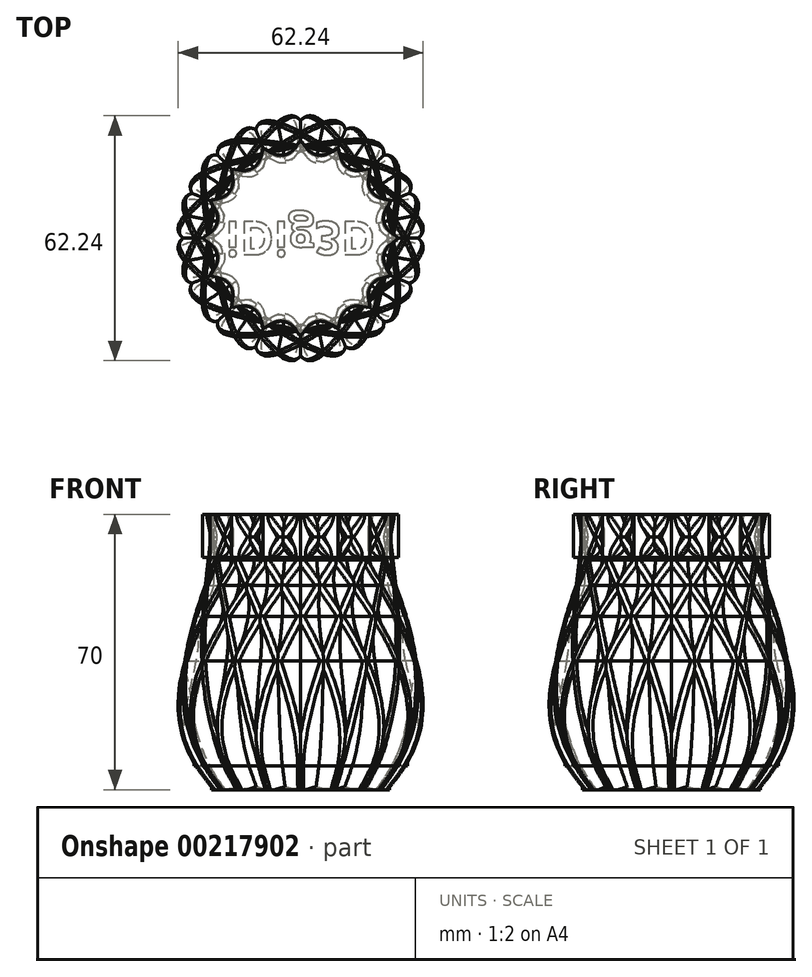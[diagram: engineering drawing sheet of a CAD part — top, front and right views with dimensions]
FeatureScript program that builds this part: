
annotation { "Feature Type Name" : "Feature", "Feature Type Description" : "" }
export const myFeature = defineFeature(function(context is Context, id is Id, definition is map)
    precondition{}
    {
        {
            var Q0;
            Q0=qCreatedBy(makeId("Top.planeOp"),FACE);
            var sketch = newSketch(context, id + "F0", { "sketchPlane" : qUnion([Q0])});
            skLineSegment(sketch, "E0", {"start": v(0, -22.6) * mm, "end": v(3.57, -17.95) * mm});
            skLineSegment(sketch, "E1.MirrorCS", {"start": v(0, -22.6) * mm, "end": v(-3.57, -17.95) * mm});
            skLineSegment(sketch, "E2", {"start": v(-2, -20) * mm, "end": v(2, -20) * mm, "construction": true});
            skPoint(sketch, "E3.orphan", {"position": v(2, -20) * mm});
            skPoint(sketch, "E4.orphan", {"position": v(-2, -20) * mm});
            skLineSegment(sketch, "E5.1.0", {"start": v(8.65, -20.89) * mm, "end": v(3.57, -17.95) * mm});
            skLineSegment(sketch, "E5.1.1", {"start": v(8.65, -20.89) * mm, "end": v(10.17, -15.22) * mm});
            skPoint(sketch, "E5.1.2", {"position": v(5.8, -19.24) * mm});
            skPoint(sketch, "E5.1.3", {"position": v(9.5, -17.71) * mm});
            skLineSegment(sketch, "E5.2.0", {"start": v(15.99, -15.99) * mm, "end": v(10.17, -15.22) * mm});
            skLineSegment(sketch, "E5.2.1", {"start": v(15.99, -15.99) * mm, "end": v(15.22, -10.17) * mm});
            skPoint(sketch, "E5.2.2", {"position": v(12.73, -15.56) * mm});
            skPoint(sketch, "E5.2.3", {"position": v(15.56, -12.73) * mm});
            skLineSegment(sketch, "E5.3.0", {"start": v(20.89, -8.65) * mm, "end": v(15.22, -10.17) * mm});
            skLineSegment(sketch, "E5.3.1", {"start": v(20.89, -8.65) * mm, "end": v(17.95, -3.57) * mm});
            skPoint(sketch, "E5.3.2", {"position": v(17.71, -9.5) * mm});
            skPoint(sketch, "E5.3.3", {"position": v(19.24, -5.8) * mm});
            skLineSegment(sketch, "E5.4.0", {"start": v(22.6, 0) * mm, "end": v(17.95, -3.57) * mm});
            skLineSegment(sketch, "E5.4.1", {"start": v(22.6, 0) * mm, "end": v(17.95, 3.57) * mm});
            skPoint(sketch, "E5.4.2", {"position": v(20, -2) * mm});
            skPoint(sketch, "E5.4.3", {"position": v(20, 2) * mm});
            skLineSegment(sketch, "E5.5.0", {"start": v(20.89, 8.65) * mm, "end": v(17.95, 3.57) * mm});
            skLineSegment(sketch, "E5.5.1", {"start": v(20.89, 8.65) * mm, "end": v(15.22, 10.17) * mm});
            skPoint(sketch, "E5.5.2", {"position": v(19.24, 5.8) * mm});
            skPoint(sketch, "E5.5.3", {"position": v(17.71, 9.5) * mm});
            skLineSegment(sketch, "E5.6.0", {"start": v(15.99, 15.99) * mm, "end": v(15.22, 10.17) * mm});
            skLineSegment(sketch, "E5.6.1", {"start": v(15.99, 15.99) * mm, "end": v(10.17, 15.22) * mm});
            skPoint(sketch, "E5.6.2", {"position": v(15.56, 12.73) * mm});
            skPoint(sketch, "E5.6.3", {"position": v(12.73, 15.56) * mm});
            skLineSegment(sketch, "E5.7.0", {"start": v(8.65, 20.89) * mm, "end": v(10.17, 15.22) * mm});
            skLineSegment(sketch, "E5.7.1", {"start": v(8.65, 20.89) * mm, "end": v(3.57, 17.95) * mm});
            skPoint(sketch, "E5.7.2", {"position": v(9.5, 17.71) * mm});
            skPoint(sketch, "E5.7.3", {"position": v(5.8, 19.24) * mm});
            skLineSegment(sketch, "E5.8.0", {"start": v(0, 22.6) * mm, "end": v(3.57, 17.95) * mm});
            skLineSegment(sketch, "E5.8.1", {"start": v(0, 22.6) * mm, "end": v(-3.57, 17.95) * mm});
            skPoint(sketch, "E5.8.2", {"position": v(2, 20) * mm});
            skPoint(sketch, "E5.8.3", {"position": v(-2, 20) * mm});
            skLineSegment(sketch, "E5.9.0", {"start": v(-8.65, 20.89) * mm, "end": v(-3.57, 17.95) * mm});
            skLineSegment(sketch, "E5.9.1", {"start": v(-8.65, 20.89) * mm, "end": v(-10.17, 15.22) * mm});
            skPoint(sketch, "E5.9.2", {"position": v(-5.8, 19.24) * mm});
            skPoint(sketch, "E5.9.3", {"position": v(-9.5, 17.71) * mm});
            skLineSegment(sketch, "E5.10.0", {"start": v(-15.99, 15.99) * mm, "end": v(-10.17, 15.22) * mm});
            skLineSegment(sketch, "E5.10.1", {"start": v(-15.99, 15.99) * mm, "end": v(-15.22, 10.17) * mm});
            skPoint(sketch, "E5.10.2", {"position": v(-12.73, 15.56) * mm});
            skPoint(sketch, "E5.10.3", {"position": v(-15.56, 12.73) * mm});
            skLineSegment(sketch, "E5.11.0", {"start": v(-20.89, 8.65) * mm, "end": v(-15.22, 10.17) * mm});
            skLineSegment(sketch, "E5.11.1", {"start": v(-20.89, 8.65) * mm, "end": v(-17.95, 3.57) * mm});
            skPoint(sketch, "E5.11.2", {"position": v(-17.71, 9.5) * mm});
            skPoint(sketch, "E5.11.3", {"position": v(-19.24, 5.8) * mm});
            skLineSegment(sketch, "E5.12.0", {"start": v(-22.6, 0) * mm, "end": v(-17.95, 3.57) * mm});
            skLineSegment(sketch, "E5.12.1", {"start": v(-22.6, 0) * mm, "end": v(-17.95, -3.57) * mm});
            skPoint(sketch, "E5.12.2", {"position": v(-20, 2) * mm});
            skPoint(sketch, "E5.12.3", {"position": v(-20, -2) * mm});
            skLineSegment(sketch, "E5.13.0", {"start": v(-20.89, -8.65) * mm, "end": v(-17.95, -3.57) * mm});
            skLineSegment(sketch, "E5.13.1", {"start": v(-20.89, -8.65) * mm, "end": v(-15.22, -10.17) * mm});
            skPoint(sketch, "E5.13.2", {"position": v(-19.24, -5.8) * mm});
            skPoint(sketch, "E5.13.3", {"position": v(-17.71, -9.5) * mm});
            skLineSegment(sketch, "E5.14.0", {"start": v(-15.99, -15.99) * mm, "end": v(-15.22, -10.17) * mm});
            skLineSegment(sketch, "E5.14.1", {"start": v(-15.99, -15.99) * mm, "end": v(-10.17, -15.22) * mm});
            skPoint(sketch, "E5.14.2", {"position": v(-15.56, -12.73) * mm});
            skPoint(sketch, "E5.14.3", {"position": v(-12.73, -15.56) * mm});
            skLineSegment(sketch, "E5.15.0", {"start": v(-8.65, -20.89) * mm, "end": v(-10.17, -15.22) * mm});
            skLineSegment(sketch, "E5.15.1", {"start": v(-8.65, -20.89) * mm, "end": v(-3.57, -17.95) * mm});
            skPoint(sketch, "E5.15.2", {"position": v(-9.5, -17.71) * mm});
            skPoint(sketch, "E5.15.3", {"position": v(-5.8, -19.24) * mm});
            skPoint(sketch, "E5.center", {"position": v(0, 0) * mm});
            skSolve(sketch);
        }
        {
            var Q0;
            Q0=qSketchRegion(id+"F0",true);
            var Q1;
            Q1=sQuery(id+"F0.wireOp",EDGE,"1b0f9fb0-313e-4c25-a7f3-239414019b98.12.0");
            var Q2;
            Q2=sQuery(id+"F0.wireOp",EDGE,"1b0f9fb0-313e-4c25-a7f3-239414019b98.13.0");
            var Q3;
            Q3=sQuery(id+"F0.wireOp",EDGE,"1b0f9fb0-313e-4c25-a7f3-239414019b98.14.0");
            var Q4;
            Q4=sQuery(id+"F0.wireOp",EDGE,"cSzGq71W-xBtn-32TR-Fl9i-aVuZMrbFhdef");
            var Q5;
            Q5=sQuery(id+"F0.wireOp",EDGE,"1b0f9fb0-313e-4c25-a7f3-239414019b98.1.0");
            var Q6;
            Q6=sQuery(id+"F0.wireOp",EDGE,"1b0f9fb0-313e-4c25-a7f3-239414019b98.2.0");
            var Q7;
            Q7=sQuery(id+"F0.wireOp",EDGE,"1b0f9fb0-313e-4c25-a7f3-239414019b98.3.0");
            var Q8;
            Q8=sQuery(id+"F0.wireOp",EDGE,"1b0f9fb0-313e-4c25-a7f3-239414019b98.4.0");
            var Q9;
            Q9=sQuery(id+"F0.wireOp",EDGE,"1b0f9fb0-313e-4c25-a7f3-239414019b98.5.0");
            var Q10;
            Q10=sQuery(id+"F0.wireOp",EDGE,"1b0f9fb0-313e-4c25-a7f3-239414019b98.6.0");
            var Q11;
            Q11=sQuery(id+"F0.wireOp",EDGE,"1b0f9fb0-313e-4c25-a7f3-239414019b98.7.0");
            var Q12;
            Q12=sQuery(id+"F0.wireOp",EDGE,"1b0f9fb0-313e-4c25-a7f3-239414019b98.8.0");
            var Q13;
            Q13=sQuery(id+"F0.wireOp",EDGE,"1b0f9fb0-313e-4c25-a7f3-239414019b98.9.0");
            var Q14;
            Q14=sQuery(id+"F0.wireOp",EDGE,"1b0f9fb0-313e-4c25-a7f3-239414019b98.10.0");
            var Q15;
            Q15=sQuery(id+"F0.wireOp",EDGE,"1b0f9fb0-313e-4c25-a7f3-239414019b98.11.0");
            var Q16;
            Q16=sQuery(id+"F0.wireOp",EDGE,"1b0f9fb0-313e-4c25-a7f3-239414019b98.15.0");
            var Q17;
            Q17=sQuery(id+"F0.wireOp",EDGE,"jFGbZxWp-MTVa-Zhwl-fwm2-ItDZcObQq6kR");
            extrude(context, id + "F1", {"entities" : qUnion([Q0]), "surfaceEntities" : qUnion([Q1, Q2, Q3, Q4, Q5, Q6, Q7, Q8, Q9, Q10, Q11, Q12, Q13, Q14, Q15, Q16, Q17]), "depth" : 10 * mm});
        }
        {
            var Q0;
            Q0=makeQuery(id+"F1.opExtrude","SWEPT_EDGE",EDGE,{"disambiguationData":[OSD([sQuery(id+"F0.wireOp",EDGE,"E5.9.1"),sQuery(id+"F0.wireOp",EDGE,"E5.10.0")])]});
            var Q1;
            Q1=makeQuery(id+"F1.opExtrude","SWEPT_EDGE",EDGE,{"disambiguationData":[OSD([sQuery(id+"F0.wireOp",EDGE,"E5.10.1"),sQuery(id+"F0.wireOp",EDGE,"E5.11.0")])]});
            var Q2;
            Q2=makeQuery(id+"F1.opExtrude","SWEPT_EDGE",EDGE,{"disambiguationData":[OSD([sQuery(id+"F0.wireOp",EDGE,"E5.8.1"),sQuery(id+"F0.wireOp",EDGE,"E5.9.0")])]});
            var Q3;
            Q3=makeQuery(id+"F1.opExtrude","SWEPT_EDGE",EDGE,{"disambiguationData":[OSD([sQuery(id+"F0.wireOp",EDGE,"E5.7.1"),sQuery(id+"F0.wireOp",EDGE,"E5.8.0")])]});
            var Q4;
            Q4=makeQuery(id+"F1.opExtrude","SWEPT_EDGE",EDGE,{"disambiguationData":[OSD([sQuery(id+"F0.wireOp",EDGE,"E5.6.1"),sQuery(id+"F0.wireOp",EDGE,"E5.7.0")])]});
            var Q5;
            Q5=makeQuery(id+"F1.opExtrude","SWEPT_EDGE",EDGE,{"disambiguationData":[OSD([sQuery(id+"F0.wireOp",EDGE,"E5.5.1"),sQuery(id+"F0.wireOp",EDGE,"E5.6.0")])]});
            var Q6;
            Q6=makeQuery(id+"F1.opExtrude","SWEPT_EDGE",EDGE,{"disambiguationData":[OSD([sQuery(id+"F0.wireOp",EDGE,"E5.4.1"),sQuery(id+"F0.wireOp",EDGE,"E5.5.0")])]});
            var Q7;
            Q7=makeQuery(id+"F1.opExtrude","SWEPT_EDGE",EDGE,{"disambiguationData":[OSD([sQuery(id+"F0.wireOp",EDGE,"E5.3.1"),sQuery(id+"F0.wireOp",EDGE,"E5.4.0")])]});
            var Q8;
            Q8=makeQuery(id+"F1.opExtrude","SWEPT_EDGE",EDGE,{"disambiguationData":[OSD([sQuery(id+"F0.wireOp",EDGE,"E5.2.1"),sQuery(id+"F0.wireOp",EDGE,"E5.3.0")])]});
            var Q9;
            Q9=makeQuery(id+"F1.opExtrude","SWEPT_EDGE",EDGE,{"disambiguationData":[OSD([sQuery(id+"F0.wireOp",EDGE,"E0"),sQuery(id+"F0.wireOp",EDGE,"E5.1.0")])]});
            var Q10;
            Q10=makeQuery(id+"F1.opExtrude","SWEPT_EDGE",EDGE,{"disambiguationData":[OSD([sQuery(id+"F0.wireOp",EDGE,"E1.MirrorCS"),sQuery(id+"F0.wireOp",EDGE,"E5.15.1")])]});
            var Q11;
            Q11=makeQuery(id+"F1.opExtrude","SWEPT_EDGE",EDGE,{"disambiguationData":[OSD([sQuery(id+"F0.wireOp",EDGE,"E5.14.1"),sQuery(id+"F0.wireOp",EDGE,"E5.15.0")])]});
            var Q12;
            Q12=makeQuery(id+"F1.opExtrude","SWEPT_EDGE",EDGE,{"disambiguationData":[OSD([sQuery(id+"F0.wireOp",EDGE,"E5.13.1"),sQuery(id+"F0.wireOp",EDGE,"E5.14.0")])]});
            var Q13;
            Q13=makeQuery(id+"F1.opExtrude","SWEPT_EDGE",EDGE,{"disambiguationData":[OSD([sQuery(id+"F0.wireOp",EDGE,"E5.12.1"),sQuery(id+"F0.wireOp",EDGE,"E5.13.0")])]});
            var Q14;
            Q14=makeQuery(id+"F1.opExtrude","SWEPT_EDGE",EDGE,{"disambiguationData":[OSD([sQuery(id+"F0.wireOp",EDGE,"E5.11.1"),sQuery(id+"F0.wireOp",EDGE,"E5.12.0")])]});
            var Q15;
            Q15=makeQuery(id+"F1.opExtrude","SWEPT_EDGE",EDGE,{"disambiguationData":[OSD([sQuery(id+"F0.wireOp",EDGE,"E5.1.1"),sQuery(id+"F0.wireOp",EDGE,"E5.2.0")])]});
            fillet(context, id + "F2", {"entities" : qUnion([Q0, Q1, Q2, Q3, Q4, Q5, Q6, Q7, Q8, Q9, Q10, Q11, Q12, Q13, Q14, Q15]), "radius" : 4 * mm, "tangentPropagation" : true, "allowEdgeOverflow" : false});
        }
        {
            var Q0;
            Q0=makeQuery(id+"F1.opExtrude","SWEPT_BODY",BODY,{"disambiguationData":[OSD([sQuery(id+"F0.wireOp",EDGE,"E0"),sQuery(id+"F0.wireOp",EDGE,"E1.MirrorCS"),sQuery(id+"F0.wireOp",EDGE,"E5.1.0"),sQuery(id+"F0.wireOp",EDGE,"E5.1.1"),sQuery(id+"F0.wireOp",EDGE,"E5.2.0"),sQuery(id+"F0.wireOp",EDGE,"E5.2.1"),sQuery(id+"F0.wireOp",EDGE,"E5.3.0"),sQuery(id+"F0.wireOp",EDGE,"E5.3.1"),sQuery(id+"F0.wireOp",EDGE,"E5.4.0"),sQuery(id+"F0.wireOp",EDGE,"E5.4.1"),sQuery(id+"F0.wireOp",EDGE,"E5.5.0"),sQuery(id+"F0.wireOp",EDGE,"E5.5.1"),sQuery(id+"F0.wireOp",EDGE,"E5.6.0"),sQuery(id+"F0.wireOp",EDGE,"E5.6.1"),sQuery(id+"F0.wireOp",EDGE,"E5.7.0"),sQuery(id+"F0.wireOp",EDGE,"E5.7.1"),sQuery(id+"F0.wireOp",EDGE,"E5.8.0"),sQuery(id+"F0.wireOp",EDGE,"E5.8.1"),sQuery(id+"F0.wireOp",EDGE,"E5.9.0"),sQuery(id+"F0.wireOp",EDGE,"E5.9.1"),sQuery(id+"F0.wireOp",EDGE,"E5.10.0"),sQuery(id+"F0.wireOp",EDGE,"E5.10.1"),sQuery(id+"F0.wireOp",EDGE,"E5.11.0"),sQuery(id+"F0.wireOp",EDGE,"E5.11.1"),sQuery(id+"F0.wireOp",EDGE,"E5.12.0"),sQuery(id+"F0.wireOp",EDGE,"E5.12.1"),sQuery(id+"F0.wireOp",EDGE,"E5.13.0"),sQuery(id+"F0.wireOp",EDGE,"E5.13.1"),sQuery(id+"F0.wireOp",EDGE,"E5.14.0"),sQuery(id+"F0.wireOp",EDGE,"E5.14.1"),sQuery(id+"F0.wireOp",EDGE,"E5.15.0"),sQuery(id+"F0.wireOp",EDGE,"E5.15.1")])]});
            transform(context, id + "F3", {"entities" : qUnion([Q0]), "transformType" : TransformType.TRANSLATION_3D, "dx" : 0 * mm, "dy" : 0 * mm, "dz" : 5 * mm, "makeCopy" : true});
        }
        {
            var Q0;
            Q0=makeQuery(id+"F3.opPattern","COPY",BODY,{"derivedFrom":makeQuery(id+"F1.opExtrude","SWEPT_BODY",BODY,{"disambiguationData":[OSD([sQuery(id+"F0.wireOp",EDGE,"E0"),sQuery(id+"F0.wireOp",EDGE,"E1.MirrorCS"),sQuery(id+"F0.wireOp",EDGE,"E5.1.0"),sQuery(id+"F0.wireOp",EDGE,"E5.1.1"),sQuery(id+"F0.wireOp",EDGE,"E5.2.0"),sQuery(id+"F0.wireOp",EDGE,"E5.2.1"),sQuery(id+"F0.wireOp",EDGE,"E5.3.0"),sQuery(id+"F0.wireOp",EDGE,"E5.3.1"),sQuery(id+"F0.wireOp",EDGE,"E5.4.0"),sQuery(id+"F0.wireOp",EDGE,"E5.4.1"),sQuery(id+"F0.wireOp",EDGE,"E5.5.0"),sQuery(id+"F0.wireOp",EDGE,"E5.5.1"),sQuery(id+"F0.wireOp",EDGE,"E5.6.0"),sQuery(id+"F0.wireOp",EDGE,"E5.6.1"),sQuery(id+"F0.wireOp",EDGE,"E5.7.0"),sQuery(id+"F0.wireOp",EDGE,"E5.7.1"),sQuery(id+"F0.wireOp",EDGE,"E5.8.0"),sQuery(id+"F0.wireOp",EDGE,"E5.8.1"),sQuery(id+"F0.wireOp",EDGE,"E5.9.0"),sQuery(id+"F0.wireOp",EDGE,"E5.9.1"),sQuery(id+"F0.wireOp",EDGE,"E5.10.0"),sQuery(id+"F0.wireOp",EDGE,"E5.10.1"),sQuery(id+"F0.wireOp",EDGE,"E5.11.0"),sQuery(id+"F0.wireOp",EDGE,"E5.11.1"),sQuery(id+"F0.wireOp",EDGE,"E5.12.0"),sQuery(id+"F0.wireOp",EDGE,"E5.12.1"),sQuery(id+"F0.wireOp",EDGE,"E5.13.0"),sQuery(id+"F0.wireOp",EDGE,"E5.13.1"),sQuery(id+"F0.wireOp",EDGE,"E5.14.0"),sQuery(id+"F0.wireOp",EDGE,"E5.14.1"),sQuery(id+"F0.wireOp",EDGE,"E5.15.0"),sQuery(id+"F0.wireOp",EDGE,"E5.15.1")])]}),"instanceName":"1"});
            var Q1;
            Q1=qCreatedBy(makeId("Origin.pointOp"),VERTEX);
            transform(context, id + "F4", {"entities" : qUnion([Q0]), "transformType" : TransformType.SCALE_UNIFORMLY, "scale" : 1.2, "scalePoint" : qUnion([Q1]), "makeCopy" : false});
        }
        {
            var Q0;
            Q0=makeQuery(id+"F1.opExtrude","SWEPT_BODY",BODY,{"disambiguationData":[OSD([sQuery(id+"F0.wireOp",EDGE,"E0"),sQuery(id+"F0.wireOp",EDGE,"E1.MirrorCS"),sQuery(id+"F0.wireOp",EDGE,"E5.1.0"),sQuery(id+"F0.wireOp",EDGE,"E5.1.1"),sQuery(id+"F0.wireOp",EDGE,"E5.2.0"),sQuery(id+"F0.wireOp",EDGE,"E5.2.1"),sQuery(id+"F0.wireOp",EDGE,"E5.3.0"),sQuery(id+"F0.wireOp",EDGE,"E5.3.1"),sQuery(id+"F0.wireOp",EDGE,"E5.4.0"),sQuery(id+"F0.wireOp",EDGE,"E5.4.1"),sQuery(id+"F0.wireOp",EDGE,"E5.5.0"),sQuery(id+"F0.wireOp",EDGE,"E5.5.1"),sQuery(id+"F0.wireOp",EDGE,"E5.6.0"),sQuery(id+"F0.wireOp",EDGE,"E5.6.1"),sQuery(id+"F0.wireOp",EDGE,"E5.7.0"),sQuery(id+"F0.wireOp",EDGE,"E5.7.1"),sQuery(id+"F0.wireOp",EDGE,"E5.8.0"),sQuery(id+"F0.wireOp",EDGE,"E5.8.1"),sQuery(id+"F0.wireOp",EDGE,"E5.9.0"),sQuery(id+"F0.wireOp",EDGE,"E5.9.1"),sQuery(id+"F0.wireOp",EDGE,"E5.10.0"),sQuery(id+"F0.wireOp",EDGE,"E5.10.1"),sQuery(id+"F0.wireOp",EDGE,"E5.11.0"),sQuery(id+"F0.wireOp",EDGE,"E5.11.1"),sQuery(id+"F0.wireOp",EDGE,"E5.12.0"),sQuery(id+"F0.wireOp",EDGE,"E5.12.1"),sQuery(id+"F0.wireOp",EDGE,"E5.13.0"),sQuery(id+"F0.wireOp",EDGE,"E5.13.1"),sQuery(id+"F0.wireOp",EDGE,"E5.14.0"),sQuery(id+"F0.wireOp",EDGE,"E5.14.1"),sQuery(id+"F0.wireOp",EDGE,"E5.15.0"),sQuery(id+"F0.wireOp",EDGE,"E5.15.1")])]});
            transform(context, id + "F5", {"entities" : qUnion([Q0]), "transformType" : TransformType.TRANSLATION_3D, "dx" : 0 * mm, "dy" : 0 * mm, "dz" : 60 * mm, "makeCopy" : true});
        }
        {
            var Q0;
            Q0=makeQuery(id+"F5.opPattern","COPY",FACE,{"derivedFrom":makeQuery(id+"F1.opExtrude","CAP_FACE",FACE,{"disambiguationData":[OSD([sQuery(id+"F0.wireOp",EDGE,"E0"),sQuery(id+"F0.wireOp",EDGE,"E1.MirrorCS"),sQuery(id+"F0.wireOp",EDGE,"E5.1.0"),sQuery(id+"F0.wireOp",EDGE,"E5.1.1"),sQuery(id+"F0.wireOp",EDGE,"E5.2.0"),sQuery(id+"F0.wireOp",EDGE,"E5.2.1"),sQuery(id+"F0.wireOp",EDGE,"E5.3.0"),sQuery(id+"F0.wireOp",EDGE,"E5.3.1"),sQuery(id+"F0.wireOp",EDGE,"E5.4.0"),sQuery(id+"F0.wireOp",EDGE,"E5.4.1"),sQuery(id+"F0.wireOp",EDGE,"E5.5.0"),sQuery(id+"F0.wireOp",EDGE,"E5.5.1"),sQuery(id+"F0.wireOp",EDGE,"E5.6.0"),sQuery(id+"F0.wireOp",EDGE,"E5.6.1"),sQuery(id+"F0.wireOp",EDGE,"E5.7.0"),sQuery(id+"F0.wireOp",EDGE,"E5.7.1"),sQuery(id+"F0.wireOp",EDGE,"E5.8.0"),sQuery(id+"F0.wireOp",EDGE,"E5.8.1"),sQuery(id+"F0.wireOp",EDGE,"E5.9.0"),sQuery(id+"F0.wireOp",EDGE,"E5.9.1"),sQuery(id+"F0.wireOp",EDGE,"E5.10.0"),sQuery(id+"F0.wireOp",EDGE,"E5.10.1"),sQuery(id+"F0.wireOp",EDGE,"E5.11.0"),sQuery(id+"F0.wireOp",EDGE,"E5.11.1"),sQuery(id+"F0.wireOp",EDGE,"E5.12.0"),sQuery(id+"F0.wireOp",EDGE,"E5.12.1"),sQuery(id+"F0.wireOp",EDGE,"E5.13.0"),sQuery(id+"F0.wireOp",EDGE,"E5.13.1"),sQuery(id+"F0.wireOp",EDGE,"E5.14.0"),sQuery(id+"F0.wireOp",EDGE,"E5.14.1"),sQuery(id+"F0.wireOp",EDGE,"E5.15.0"),sQuery(id+"F0.wireOp",EDGE,"E5.15.1")])],"isStart":false}),"instanceName":"1"});
            var sketch = newSketch(context, id + "F6", { "sketchPlane" : qUnion([Q0])});
            skPoint(sketch, "E6.0", {"position": v(0, 0) * mm});
            skSolve(sketch);
        }
        {
            var Q0;
            Q0=makeQuery(id+"F5.opPattern","COPY",BODY,{"derivedFrom":makeQuery(id+"F1.opExtrude","SWEPT_BODY",BODY,{"disambiguationData":[OSD([sQuery(id+"F0.wireOp",EDGE,"E0"),sQuery(id+"F0.wireOp",EDGE,"E1.MirrorCS"),sQuery(id+"F0.wireOp",EDGE,"E5.1.0"),sQuery(id+"F0.wireOp",EDGE,"E5.1.1"),sQuery(id+"F0.wireOp",EDGE,"E5.2.0"),sQuery(id+"F0.wireOp",EDGE,"E5.2.1"),sQuery(id+"F0.wireOp",EDGE,"E5.3.0"),sQuery(id+"F0.wireOp",EDGE,"E5.3.1"),sQuery(id+"F0.wireOp",EDGE,"E5.4.0"),sQuery(id+"F0.wireOp",EDGE,"E5.4.1"),sQuery(id+"F0.wireOp",EDGE,"E5.5.0"),sQuery(id+"F0.wireOp",EDGE,"E5.5.1"),sQuery(id+"F0.wireOp",EDGE,"E5.6.0"),sQuery(id+"F0.wireOp",EDGE,"E5.6.1"),sQuery(id+"F0.wireOp",EDGE,"E5.7.0"),sQuery(id+"F0.wireOp",EDGE,"E5.7.1"),sQuery(id+"F0.wireOp",EDGE,"E5.8.0"),sQuery(id+"F0.wireOp",EDGE,"E5.8.1"),sQuery(id+"F0.wireOp",EDGE,"E5.9.0"),sQuery(id+"F0.wireOp",EDGE,"E5.9.1"),sQuery(id+"F0.wireOp",EDGE,"E5.10.0"),sQuery(id+"F0.wireOp",EDGE,"E5.10.1"),sQuery(id+"F0.wireOp",EDGE,"E5.11.0"),sQuery(id+"F0.wireOp",EDGE,"E5.11.1"),sQuery(id+"F0.wireOp",EDGE,"E5.12.0"),sQuery(id+"F0.wireOp",EDGE,"E5.12.1"),sQuery(id+"F0.wireOp",EDGE,"E5.13.0"),sQuery(id+"F0.wireOp",EDGE,"E5.13.1"),sQuery(id+"F0.wireOp",EDGE,"E5.14.0"),sQuery(id+"F0.wireOp",EDGE,"E5.14.1"),sQuery(id+"F0.wireOp",EDGE,"E5.15.0"),sQuery(id+"F0.wireOp",EDGE,"E5.15.1")])]}),"instanceName":"1"});
            var Q1;
            Q1=sQuery(id+"F6.wireOp",VERTEX,"E6.0");
            transform(context, id + "F7", {"entities" : qUnion([Q0]), "transformType" : TransformType.SCALE_UNIFORMLY, "scale" : 1.1, "scalePoint" : qUnion([Q1]), "makeCopy" : false});
        }
        {
            var Q0;
            Q0=makeQuery(id+"F1.opExtrude","CAP_FACE",FACE,{"disambiguationData":[OSD([sQuery(id+"F0.wireOp",EDGE,"E0"),sQuery(id+"F0.wireOp",EDGE,"E1.MirrorCS"),sQuery(id+"F0.wireOp",EDGE,"E5.1.0"),sQuery(id+"F0.wireOp",EDGE,"E5.1.1"),sQuery(id+"F0.wireOp",EDGE,"E5.2.0"),sQuery(id+"F0.wireOp",EDGE,"E5.2.1"),sQuery(id+"F0.wireOp",EDGE,"E5.3.0"),sQuery(id+"F0.wireOp",EDGE,"E5.3.1"),sQuery(id+"F0.wireOp",EDGE,"E5.4.0"),sQuery(id+"F0.wireOp",EDGE,"E5.4.1"),sQuery(id+"F0.wireOp",EDGE,"E5.5.0"),sQuery(id+"F0.wireOp",EDGE,"E5.5.1"),sQuery(id+"F0.wireOp",EDGE,"E5.6.0"),sQuery(id+"F0.wireOp",EDGE,"E5.6.1"),sQuery(id+"F0.wireOp",EDGE,"E5.7.0"),sQuery(id+"F0.wireOp",EDGE,"E5.7.1"),sQuery(id+"F0.wireOp",EDGE,"E5.8.0"),sQuery(id+"F0.wireOp",EDGE,"E5.8.1"),sQuery(id+"F0.wireOp",EDGE,"E5.9.0"),sQuery(id+"F0.wireOp",EDGE,"E5.9.1"),sQuery(id+"F0.wireOp",EDGE,"E5.10.0"),sQuery(id+"F0.wireOp",EDGE,"E5.10.1"),sQuery(id+"F0.wireOp",EDGE,"E5.11.0"),sQuery(id+"F0.wireOp",EDGE,"E5.11.1"),sQuery(id+"F0.wireOp",EDGE,"E5.12.0"),sQuery(id+"F0.wireOp",EDGE,"E5.12.1"),sQuery(id+"F0.wireOp",EDGE,"E5.13.0"),sQuery(id+"F0.wireOp",EDGE,"E5.13.1"),sQuery(id+"F0.wireOp",EDGE,"E5.14.0"),sQuery(id+"F0.wireOp",EDGE,"E5.14.1"),sQuery(id+"F0.wireOp",EDGE,"E5.15.0"),sQuery(id+"F0.wireOp",EDGE,"E5.15.1")])],"isStart":true});
            var Q1;
            Q1=makeQuery(id+"F3.opPattern","COPY",FACE,{"derivedFrom":makeQuery(id+"F1.opExtrude","CAP_FACE",FACE,{"disambiguationData":[OSD([sQuery(id+"F0.wireOp",EDGE,"E0"),sQuery(id+"F0.wireOp",EDGE,"E1.MirrorCS"),sQuery(id+"F0.wireOp",EDGE,"E5.1.0"),sQuery(id+"F0.wireOp",EDGE,"E5.1.1"),sQuery(id+"F0.wireOp",EDGE,"E5.2.0"),sQuery(id+"F0.wireOp",EDGE,"E5.2.1"),sQuery(id+"F0.wireOp",EDGE,"E5.3.0"),sQuery(id+"F0.wireOp",EDGE,"E5.3.1"),sQuery(id+"F0.wireOp",EDGE,"E5.4.0"),sQuery(id+"F0.wireOp",EDGE,"E5.4.1"),sQuery(id+"F0.wireOp",EDGE,"E5.5.0"),sQuery(id+"F0.wireOp",EDGE,"E5.5.1"),sQuery(id+"F0.wireOp",EDGE,"E5.6.0"),sQuery(id+"F0.wireOp",EDGE,"E5.6.1"),sQuery(id+"F0.wireOp",EDGE,"E5.7.0"),sQuery(id+"F0.wireOp",EDGE,"E5.7.1"),sQuery(id+"F0.wireOp",EDGE,"E5.8.0"),sQuery(id+"F0.wireOp",EDGE,"E5.8.1"),sQuery(id+"F0.wireOp",EDGE,"E5.9.0"),sQuery(id+"F0.wireOp",EDGE,"E5.9.1"),sQuery(id+"F0.wireOp",EDGE,"E5.10.0"),sQuery(id+"F0.wireOp",EDGE,"E5.10.1"),sQuery(id+"F0.wireOp",EDGE,"E5.11.0"),sQuery(id+"F0.wireOp",EDGE,"E5.11.1"),sQuery(id+"F0.wireOp",EDGE,"E5.12.0"),sQuery(id+"F0.wireOp",EDGE,"E5.12.1"),sQuery(id+"F0.wireOp",EDGE,"E5.13.0"),sQuery(id+"F0.wireOp",EDGE,"E5.13.1"),sQuery(id+"F0.wireOp",EDGE,"E5.14.0"),sQuery(id+"F0.wireOp",EDGE,"E5.14.1"),sQuery(id+"F0.wireOp",EDGE,"E5.15.0"),sQuery(id+"F0.wireOp",EDGE,"E5.15.1")])],"isStart":true}),"instanceName":"1"});
            var Q2;
            Q2=makeQuery(id+"F5.opPattern","COPY",FACE,{"derivedFrom":makeQuery(id+"F1.opExtrude","CAP_FACE",FACE,{"disambiguationData":[OSD([sQuery(id+"F0.wireOp",EDGE,"E0"),sQuery(id+"F0.wireOp",EDGE,"E1.MirrorCS"),sQuery(id+"F0.wireOp",EDGE,"E5.1.0"),sQuery(id+"F0.wireOp",EDGE,"E5.1.1"),sQuery(id+"F0.wireOp",EDGE,"E5.2.0"),sQuery(id+"F0.wireOp",EDGE,"E5.2.1"),sQuery(id+"F0.wireOp",EDGE,"E5.3.0"),sQuery(id+"F0.wireOp",EDGE,"E5.3.1"),sQuery(id+"F0.wireOp",EDGE,"E5.4.0"),sQuery(id+"F0.wireOp",EDGE,"E5.4.1"),sQuery(id+"F0.wireOp",EDGE,"E5.5.0"),sQuery(id+"F0.wireOp",EDGE,"E5.5.1"),sQuery(id+"F0.wireOp",EDGE,"E5.6.0"),sQuery(id+"F0.wireOp",EDGE,"E5.6.1"),sQuery(id+"F0.wireOp",EDGE,"E5.7.0"),sQuery(id+"F0.wireOp",EDGE,"E5.7.1"),sQuery(id+"F0.wireOp",EDGE,"E5.8.0"),sQuery(id+"F0.wireOp",EDGE,"E5.8.1"),sQuery(id+"F0.wireOp",EDGE,"E5.9.0"),sQuery(id+"F0.wireOp",EDGE,"E5.9.1"),sQuery(id+"F0.wireOp",EDGE,"E5.10.0"),sQuery(id+"F0.wireOp",EDGE,"E5.10.1"),sQuery(id+"F0.wireOp",EDGE,"E5.11.0"),sQuery(id+"F0.wireOp",EDGE,"E5.11.1"),sQuery(id+"F0.wireOp",EDGE,"E5.12.0"),sQuery(id+"F0.wireOp",EDGE,"E5.12.1"),sQuery(id+"F0.wireOp",EDGE,"E5.13.0"),sQuery(id+"F0.wireOp",EDGE,"E5.13.1"),sQuery(id+"F0.wireOp",EDGE,"E5.14.0"),sQuery(id+"F0.wireOp",EDGE,"E5.14.1"),sQuery(id+"F0.wireOp",EDGE,"E5.15.0"),sQuery(id+"F0.wireOp",EDGE,"E5.15.1")])],"isStart":false}),"instanceName":"1"});
            var Q3;
            Q3=sQuery(id+"F0.wireOp",VERTEX,"E5.2.1.start");
            var Q4;
            Q4=makeQuery(id+"F3.opPattern","COPY",VERTEX,{"derivedFrom":makeQuery(id+"F1.opExtrude","CAP_VERTEX",VERTEX,{"disambiguationData":[OSD([sQuery(id+"F0.wireOp",EDGE,"E5.2.0"),sQuery(id+"F0.wireOp",EDGE,"E5.2.1")])],"isStart":true}),"instanceName":"1"});
            var Q5;
            Q5=makeQuery(id+"F5.opPattern","COPY",VERTEX,{"derivedFrom":makeQuery(id+"F1.opExtrude","CAP_VERTEX",VERTEX,{"disambiguationData":[OSD([sQuery(id+"F0.wireOp",EDGE,"E5.15.0"),sQuery(id+"F0.wireOp",EDGE,"E5.15.1")])],"isStart":false}),"instanceName":"1"});
            loft(context, id + "F8", {"sheetProfilesArray" : [{ "sheetProfileEntities" : qUnion([Q0]) }, { "sheetProfileEntities" : qUnion([Q1]) }, { "sheetProfileEntities" : qUnion([Q2]) }], "matchConnections" : true, "connections" : [{ "connectionEntities" : qUnion([Q3, Q4, Q5]), "connectionEdgeQueries" : qUnion([]), "connectionEdgeParameters" : [] }]});
        }
        {
            var Q0;
            {var subQ0=sQuery(id+"F0.wireOp",EDGE,"E5.15.1");var subQ1=sQuery(id+"F0.wireOp",EDGE,"E5.15.0");var subQ2=sQuery(id+"F0.wireOp",EDGE,"E5.14.1");var subQ3=sQuery(id+"F0.wireOp",EDGE,"E5.14.0");var subQ4=sQuery(id+"F0.wireOp",EDGE,"E5.13.1");var subQ5=sQuery(id+"F0.wireOp",EDGE,"E5.13.0");var subQ6=sQuery(id+"F0.wireOp",EDGE,"E5.12.1");var subQ7=sQuery(id+"F0.wireOp",EDGE,"E5.12.0");var subQ8=sQuery(id+"F0.wireOp",EDGE,"E5.11.1");var subQ9=sQuery(id+"F0.wireOp",EDGE,"E5.11.0");var subQ10=sQuery(id+"F0.wireOp",EDGE,"E5.10.1");var subQ11=sQuery(id+"F0.wireOp",EDGE,"E5.10.0");var subQ12=sQuery(id+"F0.wireOp",EDGE,"E5.9.1");var subQ13=sQuery(id+"F0.wireOp",EDGE,"E5.9.0");var subQ14=sQuery(id+"F0.wireOp",EDGE,"E5.8.1");var subQ15=sQuery(id+"F0.wireOp",EDGE,"E5.8.0");var subQ16=sQuery(id+"F0.wireOp",EDGE,"E5.7.1");var subQ17=sQuery(id+"F0.wireOp",EDGE,"E5.7.0");var subQ18=sQuery(id+"F0.wireOp",EDGE,"E5.6.1");var subQ19=sQuery(id+"F0.wireOp",EDGE,"E5.6.0");var subQ20=sQuery(id+"F0.wireOp",EDGE,"E5.5.1");var subQ21=sQuery(id+"F0.wireOp",EDGE,"E5.5.0");var subQ22=sQuery(id+"F0.wireOp",EDGE,"E5.4.1");var subQ23=sQuery(id+"F0.wireOp",EDGE,"E5.4.0");var subQ24=sQuery(id+"F0.wireOp",EDGE,"E5.3.1");var subQ25=sQuery(id+"F0.wireOp",EDGE,"E5.3.0");var subQ26=sQuery(id+"F0.wireOp",EDGE,"E5.2.1");var subQ27=sQuery(id+"F0.wireOp",EDGE,"E5.2.0");var subQ28=sQuery(id+"F0.wireOp",EDGE,"E5.1.1");var subQ29=sQuery(id+"F0.wireOp",EDGE,"E5.1.0");var subQ30=sQuery(id+"F0.wireOp",EDGE,"E1.MirrorCS");var subQ31=sQuery(id+"F0.wireOp",EDGE,"E0");Q0=makeQuery(id+"F8.opLoft","CAP_FACE",FACE,{"disambiguationData":[OSD([subQ31,subQ30,subQ29,subQ28,subQ27,subQ26,subQ25,subQ24,subQ23,subQ22,subQ21,subQ20,subQ19,subQ18,subQ17,subQ16,subQ15,subQ14,subQ13,subQ12,subQ11,subQ10,subQ9,subQ8,subQ7,subQ6,subQ5,subQ4,subQ3,subQ2,subQ1,subQ0]),TDD([makeQuery(id+"F1.opExtrude","CAP_FACE",FACE,{"disambiguationData":[OSD([subQ31,subQ30,subQ29,subQ28,subQ27,subQ26,subQ25,subQ24,subQ23,subQ22,subQ21,subQ20,subQ19,subQ18,subQ17,subQ16,subQ15,subQ14,subQ13,subQ12,subQ11,subQ10,subQ9,subQ8,subQ7,subQ6,subQ5,subQ4,subQ3,subQ2,subQ1,subQ0])],"isStart":true})])],"isStart":true});}
            var sketch = newSketch(context, id + "F9", { "sketchPlane" : qUnion([Q0])});
            skText(sketch, "E7", { "text": "iDig3D", "fontName": "OpenSans-Bold.ttf"});
            const initialGuessF9  = {"E7": [-0.01909, -0.00425, 1, 0, 0.0085]};
            skSetInitialGuess(sketch, initialGuessF9);
            skSolve(sketch);
        }
        {
            var Q0;
            Q0=makeQuery(id+"F8.opLoft","SWEPT_EDGE",EDGE,{"disambiguationData":[OSD([sQuery(id+"F0.wireOp",EDGE,"E5.12.0"),sQuery(id+"F0.wireOp",EDGE,"E5.12.1"),sQuery(id+"F0.wireOp",EDGE,"E5.14.0"),sQuery(id+"F0.wireOp",EDGE,"E5.14.1")])]});
            var Q1;
            Q1=makeQuery(id+"F8.opLoft","SWEPT_EDGE",EDGE,{"disambiguationData":[OSD([sQuery(id+"F0.wireOp",EDGE,"E0"),sQuery(id+"F0.wireOp",EDGE,"E1.MirrorCS"),sQuery(id+"F0.wireOp",EDGE,"E5.14.0"),sQuery(id+"F0.wireOp",EDGE,"E5.14.1")])]});
            var Q2;
            Q2=makeQuery(id+"F8.opLoft","SWEPT_EDGE",EDGE,{"disambiguationData":[OSD([sQuery(id+"F0.wireOp",EDGE,"E0"),sQuery(id+"F0.wireOp",EDGE,"E1.MirrorCS"),sQuery(id+"F0.wireOp",EDGE,"E5.2.0"),sQuery(id+"F0.wireOp",EDGE,"E5.2.1")])]});
            var Q3;
            Q3=makeQuery(id+"F8.opLoft","SWEPT_EDGE",EDGE,{"disambiguationData":[OSD([sQuery(id+"F0.wireOp",EDGE,"E5.2.0"),sQuery(id+"F0.wireOp",EDGE,"E5.2.1"),sQuery(id+"F0.wireOp",EDGE,"E5.4.0"),sQuery(id+"F0.wireOp",EDGE,"E5.4.1")])]});
            var Q4;
            Q4=makeQuery(id+"F8.opLoft","SWEPT_EDGE",EDGE,{"disambiguationData":[OSD([sQuery(id+"F0.wireOp",EDGE,"E5.4.0"),sQuery(id+"F0.wireOp",EDGE,"E5.4.1"),sQuery(id+"F0.wireOp",EDGE,"E5.6.0"),sQuery(id+"F0.wireOp",EDGE,"E5.6.1")])]});
            var Q5;
            Q5=makeQuery(id+"F8.opLoft","SWEPT_EDGE",EDGE,{"disambiguationData":[OSD([sQuery(id+"F0.wireOp",EDGE,"E5.6.0"),sQuery(id+"F0.wireOp",EDGE,"E5.6.1"),sQuery(id+"F0.wireOp",EDGE,"E5.8.0"),sQuery(id+"F0.wireOp",EDGE,"E5.8.1")])]});
            var Q6;
            Q6=makeQuery(id+"F8.opLoft","SWEPT_EDGE",EDGE,{"disambiguationData":[OSD([sQuery(id+"F0.wireOp",EDGE,"E5.8.0"),sQuery(id+"F0.wireOp",EDGE,"E5.8.1"),sQuery(id+"F0.wireOp",EDGE,"E5.10.0"),sQuery(id+"F0.wireOp",EDGE,"E5.10.1")])]});
            var Q7;
            Q7=makeQuery(id+"F8.opLoft","SWEPT_EDGE",EDGE,{"disambiguationData":[OSD([sQuery(id+"F0.wireOp",EDGE,"E5.10.0"),sQuery(id+"F0.wireOp",EDGE,"E5.10.1"),sQuery(id+"F0.wireOp",EDGE,"E5.12.0"),sQuery(id+"F0.wireOp",EDGE,"E5.12.1")])]});
            fillet(context, id + "F10", {"entities" : qUnion([Q0, Q1, Q2, Q3, Q4, Q5, Q6, Q7]), "radius" : 1 * mm, "tangentPropagation" : true, "allowEdgeOverflow" : false});
        }
        {
            var Q0;
            Q0=makeQuery(id+"F8.opLoft","SWEPT_BODY",BODY,{"disambiguationData":[OSD([sQuery(id+"F0.wireOp",EDGE,"E0"),sQuery(id+"F0.wireOp",EDGE,"E1.MirrorCS"),sQuery(id+"F0.wireOp",EDGE,"E5.1.0"),sQuery(id+"F0.wireOp",EDGE,"E5.1.1"),sQuery(id+"F0.wireOp",EDGE,"E5.2.0"),sQuery(id+"F0.wireOp",EDGE,"E5.2.1"),sQuery(id+"F0.wireOp",EDGE,"E5.3.0"),sQuery(id+"F0.wireOp",EDGE,"E5.3.1"),sQuery(id+"F0.wireOp",EDGE,"E5.4.0"),sQuery(id+"F0.wireOp",EDGE,"E5.4.1"),sQuery(id+"F0.wireOp",EDGE,"E5.5.0"),sQuery(id+"F0.wireOp",EDGE,"E5.5.1"),sQuery(id+"F0.wireOp",EDGE,"E5.6.0"),sQuery(id+"F0.wireOp",EDGE,"E5.6.1"),sQuery(id+"F0.wireOp",EDGE,"E5.7.0"),sQuery(id+"F0.wireOp",EDGE,"E5.7.1"),sQuery(id+"F0.wireOp",EDGE,"E5.8.0"),sQuery(id+"F0.wireOp",EDGE,"E5.8.1"),sQuery(id+"F0.wireOp",EDGE,"E5.9.0"),sQuery(id+"F0.wireOp",EDGE,"E5.9.1"),sQuery(id+"F0.wireOp",EDGE,"E5.10.0"),sQuery(id+"F0.wireOp",EDGE,"E5.10.1"),sQuery(id+"F0.wireOp",EDGE,"E5.11.0"),sQuery(id+"F0.wireOp",EDGE,"E5.11.1"),sQuery(id+"F0.wireOp",EDGE,"E5.12.0"),sQuery(id+"F0.wireOp",EDGE,"E5.12.1"),sQuery(id+"F0.wireOp",EDGE,"E5.13.0"),sQuery(id+"F0.wireOp",EDGE,"E5.13.1"),sQuery(id+"F0.wireOp",EDGE,"E5.14.0"),sQuery(id+"F0.wireOp",EDGE,"E5.14.1"),sQuery(id+"F0.wireOp",EDGE,"E5.15.0"),sQuery(id+"F0.wireOp",EDGE,"E5.15.1")])]});
            var Q1;
            Q1=qCreatedBy(makeId("Front.planeOp"),FACE);
            mirror(context, id + "F11", {"operationType" : NewBodyOperationType.ADD, "entities" : qUnion([Q0]), "mirrorPlane" : qUnion([Q1])});
        }
        {
            var Q0;
            Q0=qSketchRegion(id+"F9",true);
            extrude(context, id + "F12", {"entities" : qUnion([Q0]), "operationType" : NewBodyOperationType.REMOVE, "oppositeDirection" : true, "depth" : .25 * mm});
        }
    });
